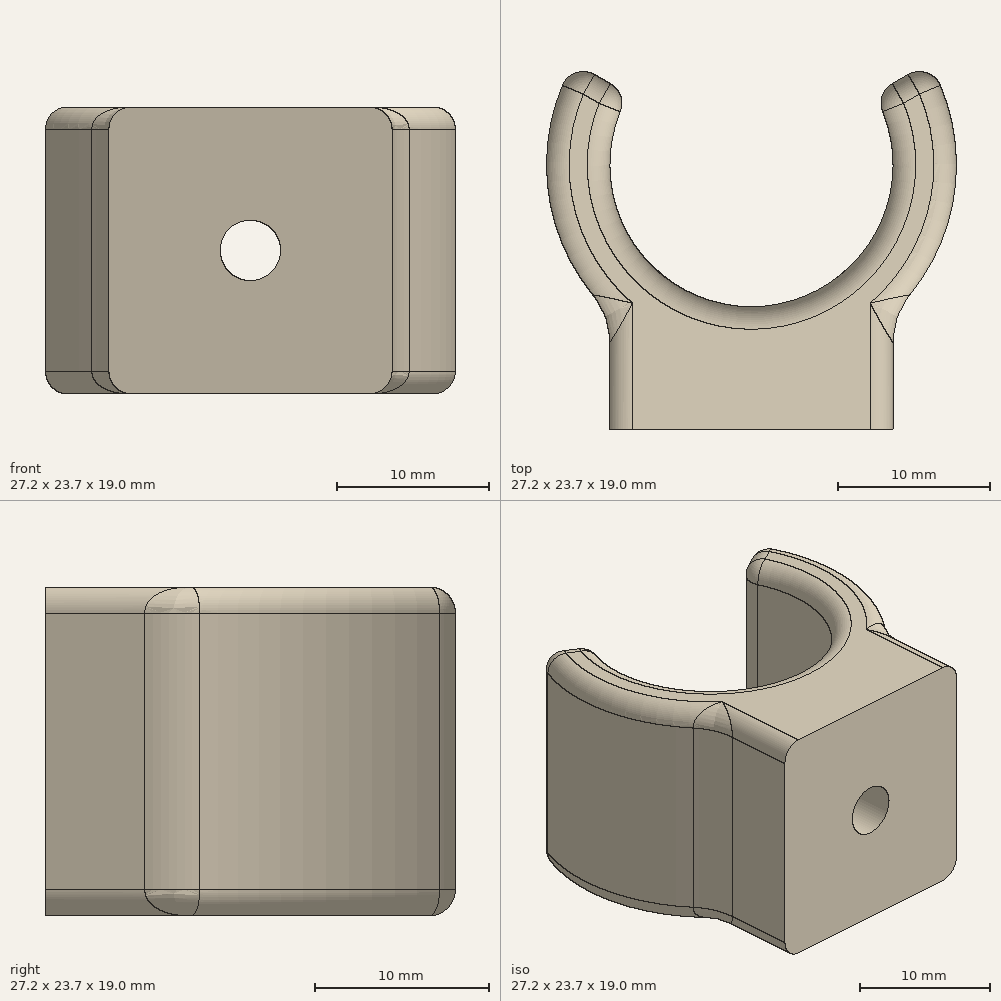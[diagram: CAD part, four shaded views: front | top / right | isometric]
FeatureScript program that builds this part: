
annotation { "Feature Type Name" : "Feature", "Feature Type Description" : "" }
export const myFeature = defineFeature(function(context is Context, id is Id, definition is map)
    precondition{}
    {
        {
            var Q0;
            Q0=qCreatedBy(makeId("Top.planeOp"),FACE);
            var sketch = newSketch(context, id + "F0", { "sketchPlane" : qUnion([Q0])});
            skLineSegment(sketch, "E0.bottom", {"start": v(9.37, -17.5) * mm, "end": v(-9.37, -17.5) * mm});
            skLineSegment(sketch, "E0.top", {"start": v(9.37, 17.5) * mm, "end": v(-9.37, 17.5) * mm, "construction": true});
            skLineSegment(sketch, "E0.left", {"start": v(9.37, -17.5) * mm, "end": v(9.37, 0) * mm});
            skLineSegment(sketch, "E0.right", {"start": v(-9.37, -17.5) * mm, "end": v(-9.37, 0) * mm});
            skPoint(sketch, "E0.middle", {"position": v(0, 0) * mm});
            skLineSegment(sketch, "E1", {"start": v(0, 0) * mm, "end": v(-11.76, 6.79) * mm, "construction": true});
            skLineSegment(sketch, "E2", {"start": v(0, 0) * mm, "end": v(18.58, 10.73) * mm, "construction": true});
            skArc(sketch, "E3", {"start": v(9.37, -9.82) * mm, "mid": v(13.44, -1.93) * mm, "end": v(11.76, 6.79) * mm});
            skArc(sketch, "E4", {"start": v(-9.37, -9.82) * mm, "mid": v(0, -13.58) * mm, "end": v(9.37, -9.82) * mm});
            skLineSegment(sketch, "E5", {"start": v(-8.12, 4.69) * mm, "end": v(-11.76, 6.79) * mm});
            skLineSegment(sketch, "E6", {"start": v(8.12, 4.69) * mm, "end": v(11.76, 6.79) * mm});
            skArc(sketch, "E7", {"start": v(11.76, 6.79) * mm, "mid": v(0, 13.58) * mm, "end": v(-11.76, 6.79) * mm, "construction": true});
            skLineSegment(sketch, "E8", {"start": v(-11.76, 6.79) * mm, "end": v(-16.82, 9.71) * mm, "construction": true});
            skArc(sketch, "E9", {"start": v(8.12, 4.69) * mm, "mid": v(0, 9.37) * mm, "end": v(-8.12, 4.69) * mm, "construction": true});
            skArc(sketch, "E10", {"start": v(-8.12, 4.69) * mm, "mid": v(0, -9.38) * mm, "end": v(8.12, 4.69) * mm});
            skArc(sketch, "E11", {"start": v(-11.76, 6.79) * mm, "mid": v(-13.44, -1.93) * mm, "end": v(-9.37, -9.82) * mm});
            skLineSegment(sketch, "E12", {"start": v(9.37, 0) * mm, "end": v(9.37, 17.5) * mm, "construction": true});
            skLineSegment(sketch, "E13", {"start": v(-9.37, 0) * mm, "end": v(-9.37, 17.5) * mm, "construction": true});
            skPoint(sketch, "E14", {"position": v(0, -9.38) * mm});
            skSolve(sketch);
        }
        {
            var Q0;
            Q0 = qSketchRegion(id + "F0", true);
            extrude(context, id + "F1", {"entities" : qUnion([Q0]), "depth" : 19 * mm, "offsetDistance" : 25 * mm});
        }
        {
            var Q0;
            Q0=makeQuery(id+"F1.opExtrude","SWEPT_FACE",FACE,{"disambiguationData":[OSD([sQuery(id+"F0.wireOp",EDGE,"E5")])]});
            var Q1;
            Q1=makeQuery(id+"F1.opExtrude","SWEPT_FACE",FACE,{"disambiguationData":[OSD([sQuery(id+"F0.wireOp",EDGE,"E6")])]});
            var Q2;
            Q2=makeQuery(id+"F1.opExtrude","CAP_EDGE",EDGE,{"disambiguationData":[OSD([sQuery(id+"F0.wireOp",EDGE,"E10")])],"isStart":false});
            var Q3;
            Q3=makeQuery(id+"F1.opExtrude","CAP_EDGE",EDGE,{"disambiguationData":[OSD([sQuery(id+"F0.wireOp",EDGE,"E10")])],"isStart":true});
            var Q4;
            Q4=makeQuery(id+"F1.opExtrude","CAP_EDGE",EDGE,{"disambiguationData":[OSD([sQuery(id+"F0.wireOp",EDGE,"E11")])],"isStart":true});
            var Q5;
            Q5=makeQuery(id+"F1.opExtrude","CAP_EDGE",EDGE,{"disambiguationData":[OSD([sQuery(id+"F0.wireOp",EDGE,"E0.right")])],"isStart":true});
            var Q6;
            Q6=makeQuery(id+"F1.opExtrude","CAP_EDGE",EDGE,{"disambiguationData":[OSD([sQuery(id+"F0.wireOp",EDGE,"E0.right")])],"isStart":false});
            var Q7;
            Q7=makeQuery(id+"F1.opExtrude","CAP_EDGE",EDGE,{"disambiguationData":[OSD([sQuery(id+"F0.wireOp",EDGE,"E11")])],"isStart":false});
            var Q8;
            Q8=makeQuery(id+"F1.opExtrude","CAP_EDGE",EDGE,{"disambiguationData":[OSD([sQuery(id+"F0.wireOp",EDGE,"E0.left")])],"isStart":false});
            var Q9;
            Q9=makeQuery(id+"F1.opExtrude","CAP_EDGE",EDGE,{"disambiguationData":[OSD([sQuery(id+"F0.wireOp",EDGE,"E3")])],"isStart":false});
            var Q10;
            Q10=makeQuery(id+"F1.opExtrude","CAP_EDGE",EDGE,{"disambiguationData":[OSD([sQuery(id+"F0.wireOp",EDGE,"E3")])],"isStart":true});
            var Q11;
            Q11=makeQuery(id+"F1.opExtrude","CAP_EDGE",EDGE,{"disambiguationData":[OSD([sQuery(id+"F0.wireOp",EDGE,"E0.left")])],"isStart":true});
            fillet(context, id + "F2", {"entities" : qUnion([Q0, Q1, Q2, Q3, Q4, Q5, Q6, Q7, Q8, Q9, Q10, Q11]), "radius" : 1.5 * mm, "tangentPropagation" : true, "allowEdgeOverflow" : false});
        }
        {
            var Q0;
            Q0=makeQuery(id+"F1.opExtrude","SWEPT_EDGE",EDGE,{"disambiguationData":[OSD([sQuery(id+"F0.wireOp",EDGE,"E0.left"),sQuery(id+"F0.wireOp",EDGE,"E3"),sQuery(id+"F0.wireOp",EDGE,"E4")])]});
            var Q1;
            Q1=makeQuery(id+"F1.opExtrude","SWEPT_EDGE",EDGE,{"disambiguationData":[OSD([sQuery(id+"F0.wireOp",EDGE,"E0.right"),sQuery(id+"F0.wireOp",EDGE,"E4"),sQuery(id+"F0.wireOp",EDGE,"E11")])]});
            fillet(context, id + "F3", {"entities" : qUnion([Q0, Q1]), "radius" : 5 * mm, "tangentPropagation" : true, "allowEdgeOverflow" : false});
        }
        {
            var Q0;
            Q0=qCreatedBy(makeId("Front.planeOp"),FACE);
            var sketch = newSketch(context, id + "F4", { "sketchPlane" : qUnion([Q0])});
            skPoint(sketch, "E15", {"position": v(0, 9.5) * mm});
            skLineSegment(sketch, "E16", {"start": v(0, 0) * mm, "end": v(0, 19) * mm, "construction": true});
            skSolve(sketch);
        }
        {
            var Q0;
            Q0=sQuery(id+"F4.wireOp",VERTEX,"E15");
            var Q1;
            Q1=makeQuery(id+"F1.opExtrude","SWEPT_BODY",BODY,{"disambiguationData":[OSD([sQuery(id+"F0.wireOp",EDGE,"E0.bottom"),sQuery(id+"F0.wireOp",EDGE,"E0.left"),sQuery(id+"F0.wireOp",EDGE,"E0.right"),sQuery(id+"F0.wireOp",EDGE,"E3"),sQuery(id+"F0.wireOp",EDGE,"E5"),sQuery(id+"F0.wireOp",EDGE,"E6"),sQuery(id+"F0.wireOp",EDGE,"E10"),sQuery(id+"F0.wireOp",EDGE,"E11")])]});
            hole(context, id + "F5", {"style" : HoleStyle.C_SINK, "endStyle" : HoleEndStyle.BLIND, "oppositeDirection" : true, "standardTappedOrClearance" : lookupTablePath({ "standard" : "ISO", "size" : "4", "type" : "Drilled" }), "standardBlindInLast" : lookupTablePath({ "standard" : "ISO", "size" : "4", "type" : "Drilled" }), "holeDiameter" : 4 * mm, "cSinkDiameter" : 11.2 * mm, "cSinkAngle" : 90 * degree, "majorDiameter" : 5 * mm, "holeDepth" : 25 * mm, "isTappedThrough" : true, "tappedDepth" : 12 * mm, "tapClearance" : 3, "locations" : qUnion([Q0]), "scope" : qUnion([Q1]), "startStyle" : HoleStartStyle.PART});
        }
    });
